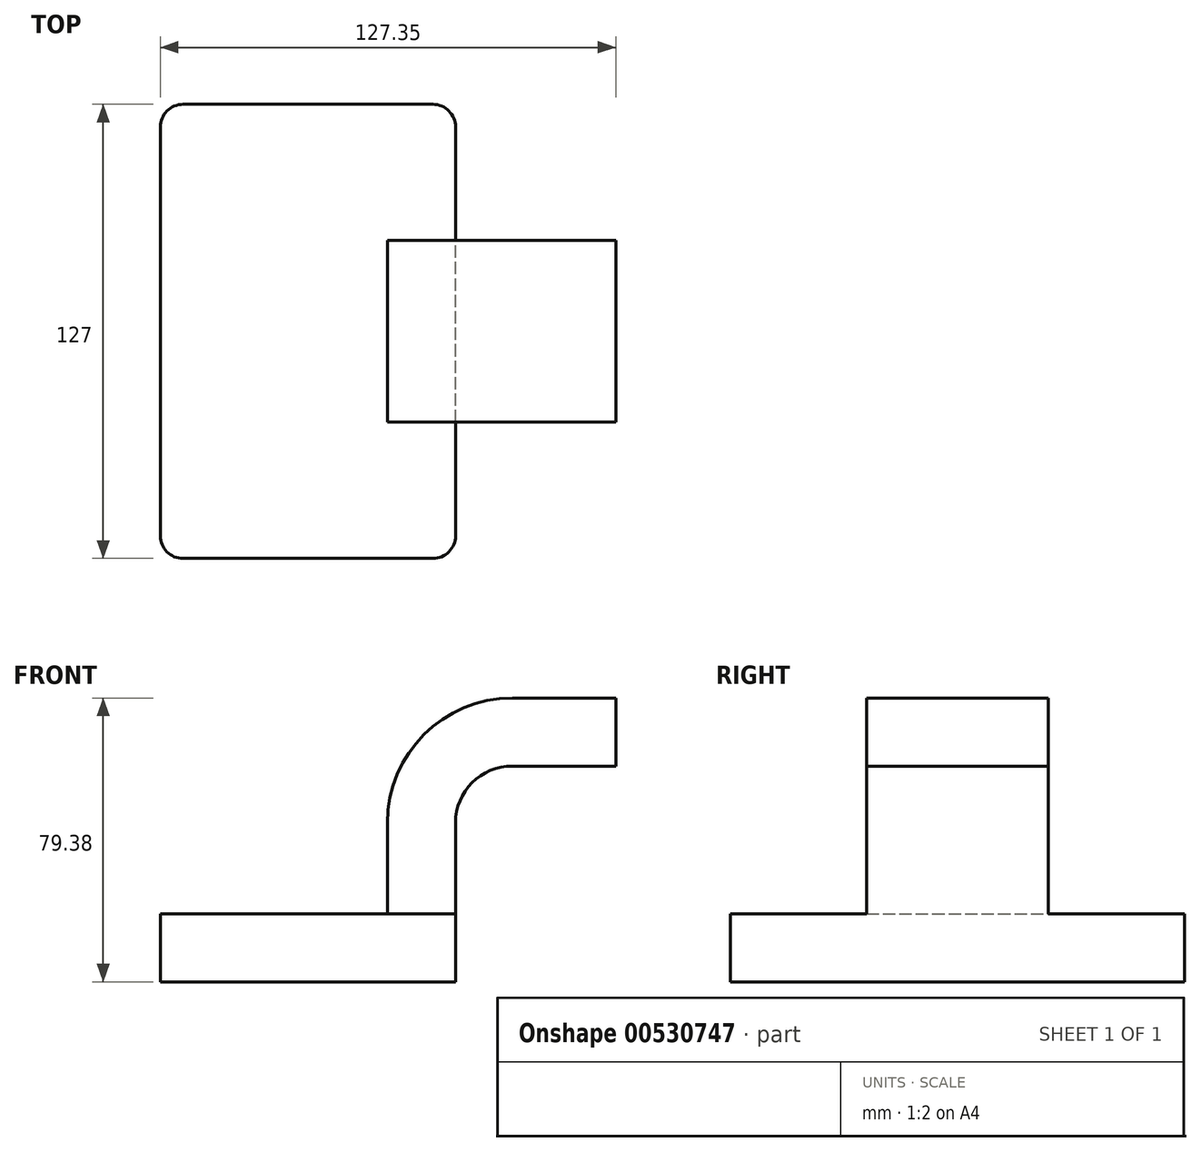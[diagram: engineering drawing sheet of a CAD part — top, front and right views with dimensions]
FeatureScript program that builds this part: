
annotation { "Feature Type Name" : "Feature", "Feature Type Description" : "" }
export const myFeature = defineFeature(function(context is Context, id is Id, definition is map)
    precondition{}
    {
        {
            var Q0;
            Q0=qCreatedBy(makeId("Front.planeOp"),FACE);
            var sketch = newSketch(context, id + "F0", { "sketchPlane" : qUnion([Q0])});
            skLineSegment(sketch, "E0.bottom", {"start": v(41.27, 9.53) * mm, "end": v(-41.28, 9.53) * mm});
            skLineSegment(sketch, "E0.top", {"start": v(41.28, -9.52) * mm, "end": v(-41.27, -9.52) * mm});
            skLineSegment(sketch, "E0.left", {"start": v(41.28, 9.53) * mm, "end": v(41.28, -9.52) * mm});
            skLineSegment(sketch, "E0.right", {"start": v(-41.28, 9.53) * mm, "end": v(-41.27, -9.52) * mm});
            skPoint(sketch, "E0.middle", {"position": v(0, 0) * mm});
            skLineSegment(sketch, "E1.bottom", {"start": v(111.12, 76.2) * mm, "end": v(60.32, 76.2) * mm});
            skLineSegment(sketch, "E1.top", {"start": v(111.12, 47.62) * mm, "end": v(60.32, 47.62) * mm});
            skLineSegment(sketch, "E1.left", {"start": v(111.12, 76.2) * mm, "end": v(111.12, 47.62) * mm});
            skLineSegment(sketch, "E1.right", {"start": v(60.32, 76.2) * mm, "end": v(60.32, 47.62) * mm});
            skPoint(sketch, "E1.middle", {"position": v(85.72, 61.91) * mm});
            skLineSegment(sketch, "E2", {"start": v(41.27, 9.53) * mm, "end": v(41.27, 34.92) * mm});
            skArc(sketch, "E3", {"start": v(41.27, 34.92) * mm, "mid": v(45.92, 46.15) * mm, "end": v(57.15, 50.8) * mm});
            skLineSegment(sketch, "E4", {"start": v(57.15, 50.8) * mm, "end": v(86.08, 50.8) * mm});
            skLineSegment(sketch, "E5.0", {"start": v(57.15, 69.85) * mm, "end": v(86.08, 69.85) * mm});
            skArc(sketch, "E5.1", {"start": v(22.23, 34.93) * mm, "mid": v(32.45, 59.62) * mm, "end": v(57.15, 69.85) * mm});
            skLineSegment(sketch, "E5.2", {"start": v(22.22, 9.53) * mm, "end": v(22.22, 34.93) * mm});
            skLineSegment(sketch, "E6", {"start": v(86.08, 50.8) * mm, "end": v(86.08, 69.85) * mm});
            skFitSpline(sketch, "E7", {"points": [v(-41.28, 9.52) * mm, v(57.15, 69.85) * mm], "startDerivative": vector(41.85, 114.73) * mm, "endDerivative": vector(114.72, -5.81) * mm});
            skSolve(sketch);
        }
        {
            var Q0;
            Q0=makeQuery(id+"F0.imprint","IMPRINT",FACE,{"disambiguationData":[TD([[makeQuery(id+"F0.imprint","IMPRINT",EDGE,{"derivedFrom":sQuery(id+"F0.wireOp",EDGE,"E0.top")}),-1.0]])]});
            extrude(context, id + "F1", {"entities" : qUnion([Q0]), "endBound" : BoundingType.SYMMETRIC, "depth" : 127 * mm, "offsetDistance" : 25.4 * mm});
        }
        {
            var Q0;
            {var subQ1=sQuery(id+"F0.wireOp",EDGE,"E2");Q0=makeQuery(id+"F0.imprint","IMPRINT",FACE,{"disambiguationData":[TD([[makeQuery(id+"F0.imprint","IMPRINT",EDGE,{"derivedFrom":subQ1}),1.0]])]});}
            var Q1;
            {var subQ5=sQuery(id+"F0.wireOp",EDGE,"E6");Q1=makeQuery(id+"F0.imprint","IMPRINT",FACE,{"disambiguationData":[TD([[makeQuery(id+"F0.imprint","IMPRINT",EDGE,{"derivedFrom":subQ5}),1.0]])]});}
            extrude(context, id + "F2", {"entities" : qUnion([Q0, Q1]), "operationType" : NewBodyOperationType.ADD, "endBound" : BoundingType.SYMMETRIC, "depth" : 50.8 * mm, "offsetDistance" : 25.4 * mm});
        }
        {
            var Q0;
            Q0=makeQuery(id+"F0.imprint","IMPRINT",FACE,{"disambiguationData":[TD([[makeQuery(id+"F0.imprint","IMPRINT",EDGE,{"derivedFrom":sQuery(id+"F0.wireOp",EDGE,"E5.1")}),1.0]])]});
            extrude(context, id + "F3", {"entities" : qUnion([Q0]), "operationType" : NewBodyOperationType.ADD, "endBound" : BoundingType.SYMMETRIC, "depth" : 15.88 * mm, "offsetDistance" : 25.4 * mm});
        }
        {
            var Q0;
            Q0=makeQuery(id+"F1.opExtrude","CAP_EDGE",EDGE,{"disambiguationData":[OSD([sQuery(id+"F0.wireOp",EDGE,"E0.left")])],"isStart":false});
            var Q1;
            Q1=makeQuery(id+"F1.opExtrude","CAP_EDGE",EDGE,{"disambiguationData":[OSD([sQuery(id+"F0.wireOp",EDGE,"E0.right")])],"isStart":false});
            var Q2;
            Q2=makeQuery(id+"F1.opExtrude","CAP_EDGE",EDGE,{"disambiguationData":[OSD([sQuery(id+"F0.wireOp",EDGE,"E0.left")])],"isStart":true});
            var Q3;
            Q3=makeQuery(id+"F1.opExtrude","CAP_EDGE",EDGE,{"disambiguationData":[OSD([sQuery(id+"F0.wireOp",EDGE,"E0.right")])],"isStart":true});
            fillet(context, id + "F4", {"entities" : qUnion([Q0, Q1, Q2, Q3]), "radius" : 6.35 * mm, "tangentPropagation" : true, "allowEdgeOverflow" : false});
        }
    });
